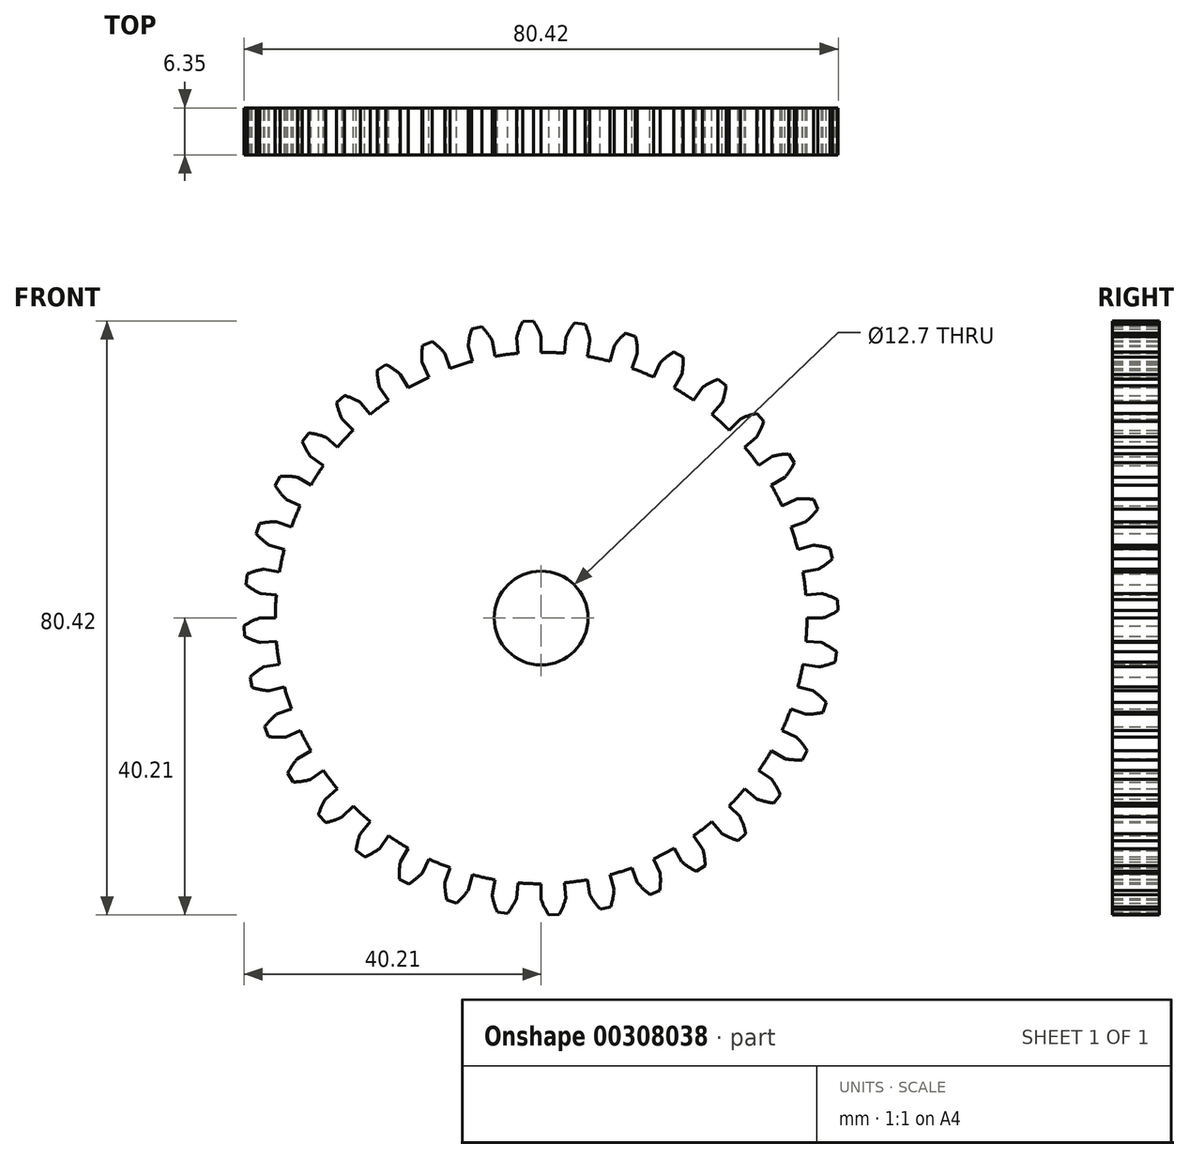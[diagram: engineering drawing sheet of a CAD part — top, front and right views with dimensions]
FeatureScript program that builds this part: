
annotation { "Feature Type Name" : "Feature", "Feature Type Description" : "" }
export const myFeature = defineFeature(function(context is Context, id is Id, definition is map)
    precondition{}
    {
        {
            var Q0;
            Q0=qCreatedBy(makeId("Front.planeOp"),FACE);
            var sketch = newSketch(context, id + "F0", { "sketchPlane" : qUnion([Q0])});
            skArc(sketch, "E0", {"start": v(-3.14, 35.84) * mm, "mid": v(-4.7, 35.67) * mm, "end": v(-6.25, 35.43) * mm});
            skPoint(sketch, "E1.endSnap0", {"position": v(0, 38.41) * mm});
            skArc(sketch, "E2.trimOffspring", {"start": v(0, 38.1) * mm, "mid": v(-0.46, 39.19) * mm, "end": v(-1.04, 40.2) * mm});
            skLineSegment(sketch, "E3", {"start": v(0, 38.1) * mm, "end": v(0, 35.98) * mm});
            skLineSegment(sketch, "E4", {"start": v(-1.04, 40.2) * mm, "end": v(-1.75, 40.18) * mm});
            skLineSegment(sketch, "E5.MirrorCS", {"start": v(-2.46, 40.15) * mm, "end": v(-1.75, 40.18) * mm});
            skArc(sketch, "E6.MirrorCS", {"start": v(-3.32, 37.96) * mm, "mid": v(-2.96, 39.08) * mm, "end": v(-2.46, 40.15) * mm});
            skLineSegment(sketch, "E7.MirrorCS", {"start": v(-3.32, 37.96) * mm, "end": v(-3.14, 35.84) * mm});
            skLineSegment(sketch, "E8.1.0", {"start": v(-9.86, 36.8) * mm, "end": v(-9.31, 34.75) * mm});
            skArc(sketch, "E8.1.1", {"start": v(-9.86, 36.8) * mm, "mid": v(-9.7, 37.97) * mm, "end": v(-9.4, 39.1) * mm});
            skLineSegment(sketch, "E8.1.2", {"start": v(-9.4, 39.1) * mm, "end": v(-8.7, 39.26) * mm});
            skLineSegment(sketch, "E8.1.3", {"start": v(-8.01, 39.42) * mm, "end": v(-8.7, 39.26) * mm});
            skArc(sketch, "E8.1.4", {"start": v(-6.62, 37.52) * mm, "mid": v(-7.25, 38.51) * mm, "end": v(-8.01, 39.42) * mm});
            skLineSegment(sketch, "E8.1.5", {"start": v(-6.62, 37.52) * mm, "end": v(-6.25, 35.43) * mm});
            skLineSegment(sketch, "E8.2.0", {"start": v(-16.1, 34.53) * mm, "end": v(-15.2, 32.6) * mm});
            skArc(sketch, "E8.2.1", {"start": v(-16.1, 34.53) * mm, "mid": v(-16.15, 35.7) * mm, "end": v(-16.05, 36.88) * mm});
            skLineSegment(sketch, "E8.2.2", {"start": v(-16.05, 36.88) * mm, "end": v(-15.39, 37.15) * mm});
            skLineSegment(sketch, "E8.2.3", {"start": v(-14.73, 37.43) * mm, "end": v(-15.39, 37.15) * mm});
            skArc(sketch, "E8.2.4", {"start": v(-13.03, 35.8) * mm, "mid": v(-13.83, 36.67) * mm, "end": v(-14.73, 37.43) * mm});
            skLineSegment(sketch, "E8.2.5", {"start": v(-13.03, 35.8) * mm, "end": v(-12.3, 33.8) * mm});
            skLineSegment(sketch, "E8.3.0", {"start": v(-21.85, 31.2) * mm, "end": v(-20.64, 29.47) * mm});
            skArc(sketch, "E8.3.1", {"start": v(-21.85, 31.2) * mm, "mid": v(-22.1, 32.36) * mm, "end": v(-22.2, 33.54) * mm});
            skLineSegment(sketch, "E8.3.2", {"start": v(-22.2, 33.54) * mm, "end": v(-21.6, 33.92) * mm});
            skLineSegment(sketch, "E8.3.3", {"start": v(-21, 34.3) * mm, "end": v(-21.6, 33.92) * mm});
            skArc(sketch, "E8.3.4", {"start": v(-19.05, 33) * mm, "mid": v(-19.99, 33.7) * mm, "end": v(-21, 34.3) * mm});
            skLineSegment(sketch, "E8.3.5", {"start": v(-19.05, 33) * mm, "end": v(-17.99, 31.16) * mm});
            skLineSegment(sketch, "E8.4.0", {"start": v(-26.94, 26.94) * mm, "end": v(-25.44, 25.44) * mm});
            skArc(sketch, "E8.4.1", {"start": v(-26.94, 26.94) * mm, "mid": v(-27.39, 28.03) * mm, "end": v(-27.7, 29.17) * mm});
            skLineSegment(sketch, "E8.4.2", {"start": v(-27.7, 29.17) * mm, "end": v(-27.17, 29.65) * mm});
            skLineSegment(sketch, "E8.4.3", {"start": v(-26.64, 30.13) * mm, "end": v(-27.17, 29.65) * mm});
            skArc(sketch, "E8.4.4", {"start": v(-24.5, 29.19) * mm, "mid": v(-25.54, 29.72) * mm, "end": v(-26.64, 30.13) * mm});
            skLineSegment(sketch, "E8.4.5", {"start": v(-24.5, 29.19) * mm, "end": v(-23.13, 27.56) * mm});
            skLineSegment(sketch, "E8.5.0", {"start": v(-31.2, 21.85) * mm, "end": v(-29.47, 20.64) * mm});
            skArc(sketch, "E8.5.1", {"start": v(-31.2, 21.85) * mm, "mid": v(-31.84, 22.85) * mm, "end": v(-32.34, 23.92) * mm});
            skLineSegment(sketch, "E8.5.2", {"start": v(-32.34, 23.92) * mm, "end": v(-31.9, 24.48) * mm});
            skLineSegment(sketch, "E8.5.3", {"start": v(-31.47, 25.04) * mm, "end": v(-31.9, 24.48) * mm});
            skArc(sketch, "E8.5.4", {"start": v(-29.19, 24.5) * mm, "mid": v(-30.31, 24.84) * mm, "end": v(-31.47, 25.04) * mm});
            skLineSegment(sketch, "E8.5.5", {"start": v(-29.19, 24.5) * mm, "end": v(-27.56, 23.13) * mm});
            skLineSegment(sketch, "E8.6.0", {"start": v(-34.53, 16.1) * mm, "end": v(-32.6, 15.2) * mm});
            skArc(sketch, "E8.6.1", {"start": v(-34.53, 16.1) * mm, "mid": v(-35.32, 16.97) * mm, "end": v(-36, 17.94) * mm});
            skLineSegment(sketch, "E8.6.2", {"start": v(-36, 17.94) * mm, "end": v(-35.67, 18.57) * mm});
            skLineSegment(sketch, "E8.6.3", {"start": v(-35.34, 19.2) * mm, "end": v(-35.67, 18.57) * mm});
            skArc(sketch, "E8.6.4", {"start": v(-33, 19.05) * mm, "mid": v(-34.16, 19.2) * mm, "end": v(-35.34, 19.2) * mm});
            skLineSegment(sketch, "E8.6.5", {"start": v(-33, 19.05) * mm, "end": v(-31.16, 17.99) * mm});
            skLineSegment(sketch, "E8.7.0", {"start": v(-36.8, 9.86) * mm, "end": v(-34.75, 9.31) * mm});
            skArc(sketch, "E8.7.1", {"start": v(-36.8, 9.86) * mm, "mid": v(-37.73, 10.58) * mm, "end": v(-38.57, 11.42) * mm});
            skLineSegment(sketch, "E8.7.2", {"start": v(-38.57, 11.42) * mm, "end": v(-38.35, 12.1) * mm});
            skLineSegment(sketch, "E8.7.3", {"start": v(-38.14, 12.77) * mm, "end": v(-38.35, 12.1) * mm});
            skArc(sketch, "E8.7.4", {"start": v(-35.8, 13.03) * mm, "mid": v(-36.98, 12.97) * mm, "end": v(-38.14, 12.77) * mm});
            skLineSegment(sketch, "E8.7.5", {"start": v(-35.8, 13.03) * mm, "end": v(-33.8, 12.3) * mm});
            skLineSegment(sketch, "E8.8.0", {"start": v(-37.96, 3.32) * mm, "end": v(-35.84, 3.14) * mm});
            skArc(sketch, "E8.8.1", {"start": v(-37.96, 3.32) * mm, "mid": v(-39, 3.87) * mm, "end": v(-39.96, 4.54) * mm});
            skLineSegment(sketch, "E8.8.2", {"start": v(-39.96, 4.54) * mm, "end": v(-39.87, 5.25) * mm});
            skLineSegment(sketch, "E8.8.3", {"start": v(-39.78, 5.95) * mm, "end": v(-39.87, 5.25) * mm});
            skArc(sketch, "E8.8.4", {"start": v(-37.52, 6.62) * mm, "mid": v(-38.67, 6.35) * mm, "end": v(-39.78, 5.95) * mm});
            skLineSegment(sketch, "E8.8.5", {"start": v(-37.52, 6.62) * mm, "end": v(-35.43, 6.25) * mm});
            skLineSegment(sketch, "E8.9.0", {"start": v(-37.96, -3.32) * mm, "end": v(-35.84, -3.14) * mm});
            skArc(sketch, "E8.9.1", {"start": v(-37.96, -3.32) * mm, "mid": v(-39.08, -2.96) * mm, "end": v(-40.15, -2.46) * mm});
            skLineSegment(sketch, "E8.9.2", {"start": v(-40.15, -2.46) * mm, "end": v(-40.18, -1.75) * mm});
            skLineSegment(sketch, "E8.9.3", {"start": v(-40.2, -1.04) * mm, "end": v(-40.18, -1.75) * mm});
            skArc(sketch, "E8.9.4", {"start": v(-38.1, 0) * mm, "mid": v(-39.19, -0.46) * mm, "end": v(-40.2, -1.04) * mm});
            skLineSegment(sketch, "E8.9.5", {"start": v(-38.1, 0) * mm, "end": v(-35.98, 0) * mm});
            skLineSegment(sketch, "E8.10.0", {"start": v(-36.8, -9.86) * mm, "end": v(-34.75, -9.31) * mm});
            skArc(sketch, "E8.10.1", {"start": v(-36.8, -9.86) * mm, "mid": v(-37.97, -9.7) * mm, "end": v(-39.1, -9.4) * mm});
            skLineSegment(sketch, "E8.10.2", {"start": v(-39.1, -9.4) * mm, "end": v(-39.26, -8.7) * mm});
            skLineSegment(sketch, "E8.10.3", {"start": v(-39.42, -8.01) * mm, "end": v(-39.26, -8.7) * mm});
            skArc(sketch, "E8.10.4", {"start": v(-37.52, -6.62) * mm, "mid": v(-38.51, -7.25) * mm, "end": v(-39.42, -8.01) * mm});
            skLineSegment(sketch, "E8.10.5", {"start": v(-37.52, -6.62) * mm, "end": v(-35.43, -6.25) * mm});
            skLineSegment(sketch, "E8.11.0", {"start": v(-34.53, -16.1) * mm, "end": v(-32.6, -15.2) * mm});
            skArc(sketch, "E8.11.1", {"start": v(-34.53, -16.1) * mm, "mid": v(-35.7, -16.15) * mm, "end": v(-36.88, -16.05) * mm});
            skLineSegment(sketch, "E8.11.2", {"start": v(-36.88, -16.05) * mm, "end": v(-37.15, -15.39) * mm});
            skLineSegment(sketch, "E8.11.3", {"start": v(-37.43, -14.73) * mm, "end": v(-37.15, -15.39) * mm});
            skArc(sketch, "E8.11.4", {"start": v(-35.8, -13.03) * mm, "mid": v(-36.67, -13.83) * mm, "end": v(-37.43, -14.73) * mm});
            skLineSegment(sketch, "E8.11.5", {"start": v(-35.8, -13.03) * mm, "end": v(-33.8, -12.3) * mm});
            skLineSegment(sketch, "E8.12.0", {"start": v(-31.2, -21.85) * mm, "end": v(-29.47, -20.64) * mm});
            skArc(sketch, "E8.12.1", {"start": v(-31.2, -21.85) * mm, "mid": v(-32.36, -22.1) * mm, "end": v(-33.54, -22.2) * mm});
            skLineSegment(sketch, "E8.12.2", {"start": v(-33.54, -22.2) * mm, "end": v(-33.92, -21.6) * mm});
            skLineSegment(sketch, "E8.12.3", {"start": v(-34.3, -21) * mm, "end": v(-33.92, -21.6) * mm});
            skArc(sketch, "E8.12.4", {"start": v(-33, -19.05) * mm, "mid": v(-33.7, -19.99) * mm, "end": v(-34.3, -21) * mm});
            skLineSegment(sketch, "E8.12.5", {"start": v(-33, -19.05) * mm, "end": v(-31.16, -17.99) * mm});
            skLineSegment(sketch, "E8.13.0", {"start": v(-26.94, -26.94) * mm, "end": v(-25.44, -25.44) * mm});
            skArc(sketch, "E8.13.1", {"start": v(-26.94, -26.94) * mm, "mid": v(-28.03, -27.39) * mm, "end": v(-29.17, -27.7) * mm});
            skLineSegment(sketch, "E8.13.2", {"start": v(-29.17, -27.7) * mm, "end": v(-29.65, -27.17) * mm});
            skLineSegment(sketch, "E8.13.3", {"start": v(-30.13, -26.64) * mm, "end": v(-29.65, -27.17) * mm});
            skArc(sketch, "E8.13.4", {"start": v(-29.19, -24.5) * mm, "mid": v(-29.72, -25.54) * mm, "end": v(-30.13, -26.64) * mm});
            skLineSegment(sketch, "E8.13.5", {"start": v(-29.19, -24.5) * mm, "end": v(-27.56, -23.13) * mm});
            skLineSegment(sketch, "E8.14.0", {"start": v(-21.85, -31.2) * mm, "end": v(-20.64, -29.47) * mm});
            skArc(sketch, "E8.14.1", {"start": v(-21.85, -31.2) * mm, "mid": v(-22.85, -31.84) * mm, "end": v(-23.92, -32.34) * mm});
            skLineSegment(sketch, "E8.14.2", {"start": v(-23.92, -32.34) * mm, "end": v(-24.48, -31.9) * mm});
            skLineSegment(sketch, "E8.14.3", {"start": v(-25.04, -31.47) * mm, "end": v(-24.48, -31.9) * mm});
            skArc(sketch, "E8.14.4", {"start": v(-24.5, -29.19) * mm, "mid": v(-24.84, -30.31) * mm, "end": v(-25.04, -31.47) * mm});
            skLineSegment(sketch, "E8.14.5", {"start": v(-24.5, -29.19) * mm, "end": v(-23.13, -27.56) * mm});
            skLineSegment(sketch, "E8.15.0", {"start": v(-16.1, -34.53) * mm, "end": v(-15.2, -32.6) * mm});
            skArc(sketch, "E8.15.1", {"start": v(-16.1, -34.53) * mm, "mid": v(-16.97, -35.32) * mm, "end": v(-17.94, -36) * mm});
            skLineSegment(sketch, "E8.15.2", {"start": v(-17.94, -36) * mm, "end": v(-18.57, -35.67) * mm});
            skLineSegment(sketch, "E8.15.3", {"start": v(-19.2, -35.34) * mm, "end": v(-18.57, -35.67) * mm});
            skArc(sketch, "E8.15.4", {"start": v(-19.05, -33) * mm, "mid": v(-19.2, -34.16) * mm, "end": v(-19.2, -35.34) * mm});
            skLineSegment(sketch, "E8.15.5", {"start": v(-19.05, -33) * mm, "end": v(-17.99, -31.16) * mm});
            skLineSegment(sketch, "E8.16.0", {"start": v(-9.86, -36.8) * mm, "end": v(-9.31, -34.75) * mm});
            skArc(sketch, "E8.16.1", {"start": v(-9.86, -36.8) * mm, "mid": v(-10.58, -37.73) * mm, "end": v(-11.42, -38.57) * mm});
            skLineSegment(sketch, "E8.16.2", {"start": v(-11.42, -38.57) * mm, "end": v(-12.1, -38.35) * mm});
            skLineSegment(sketch, "E8.16.3", {"start": v(-12.77, -38.14) * mm, "end": v(-12.1, -38.35) * mm});
            skArc(sketch, "E8.16.4", {"start": v(-13.03, -35.8) * mm, "mid": v(-12.97, -36.98) * mm, "end": v(-12.77, -38.14) * mm});
            skLineSegment(sketch, "E8.16.5", {"start": v(-13.03, -35.8) * mm, "end": v(-12.3, -33.8) * mm});
            skLineSegment(sketch, "E8.17.0", {"start": v(-3.32, -37.96) * mm, "end": v(-3.14, -35.84) * mm});
            skArc(sketch, "E8.17.1", {"start": v(-3.32, -37.96) * mm, "mid": v(-3.87, -39) * mm, "end": v(-4.54, -39.96) * mm});
            skLineSegment(sketch, "E8.17.2", {"start": v(-4.54, -39.96) * mm, "end": v(-5.25, -39.87) * mm});
            skLineSegment(sketch, "E8.17.3", {"start": v(-5.95, -39.78) * mm, "end": v(-5.25, -39.87) * mm});
            skArc(sketch, "E8.17.4", {"start": v(-6.62, -37.52) * mm, "mid": v(-6.35, -38.67) * mm, "end": v(-5.95, -39.78) * mm});
            skLineSegment(sketch, "E8.17.5", {"start": v(-6.62, -37.52) * mm, "end": v(-6.25, -35.43) * mm});
            skLineSegment(sketch, "E8.18.0", {"start": v(3.32, -37.96) * mm, "end": v(3.14, -35.84) * mm});
            skArc(sketch, "E8.18.1", {"start": v(3.32, -37.96) * mm, "mid": v(2.96, -39.08) * mm, "end": v(2.46, -40.15) * mm});
            skLineSegment(sketch, "E8.18.2", {"start": v(2.46, -40.15) * mm, "end": v(1.75, -40.18) * mm});
            skLineSegment(sketch, "E8.18.3", {"start": v(1.04, -40.2) * mm, "end": v(1.75, -40.18) * mm});
            skArc(sketch, "E8.18.4", {"start": v(0, -38.1) * mm, "mid": v(0.46, -39.19) * mm, "end": v(1.04, -40.2) * mm});
            skLineSegment(sketch, "E8.18.5", {"start": v(0, -38.1) * mm, "end": v(0, -35.98) * mm});
            skLineSegment(sketch, "E8.19.0", {"start": v(9.86, -36.8) * mm, "end": v(9.31, -34.75) * mm});
            skArc(sketch, "E8.19.1", {"start": v(9.86, -36.8) * mm, "mid": v(9.7, -37.97) * mm, "end": v(9.4, -39.1) * mm});
            skLineSegment(sketch, "E8.19.2", {"start": v(9.4, -39.1) * mm, "end": v(8.7, -39.26) * mm});
            skLineSegment(sketch, "E8.19.3", {"start": v(8.01, -39.42) * mm, "end": v(8.7, -39.26) * mm});
            skArc(sketch, "E8.19.4", {"start": v(6.62, -37.52) * mm, "mid": v(7.25, -38.51) * mm, "end": v(8.01, -39.42) * mm});
            skLineSegment(sketch, "E8.19.5", {"start": v(6.62, -37.52) * mm, "end": v(6.25, -35.43) * mm});
            skLineSegment(sketch, "E8.20.0", {"start": v(16.1, -34.53) * mm, "end": v(15.2, -32.6) * mm});
            skArc(sketch, "E8.20.1", {"start": v(16.1, -34.53) * mm, "mid": v(16.15, -35.7) * mm, "end": v(16.05, -36.88) * mm});
            skLineSegment(sketch, "E8.20.2", {"start": v(16.05, -36.88) * mm, "end": v(15.39, -37.15) * mm});
            skLineSegment(sketch, "E8.20.3", {"start": v(14.73, -37.43) * mm, "end": v(15.39, -37.15) * mm});
            skArc(sketch, "E8.20.4", {"start": v(13.03, -35.8) * mm, "mid": v(13.83, -36.67) * mm, "end": v(14.73, -37.43) * mm});
            skLineSegment(sketch, "E8.20.5", {"start": v(13.03, -35.8) * mm, "end": v(12.3, -33.8) * mm});
            skLineSegment(sketch, "E8.21.0", {"start": v(21.85, -31.2) * mm, "end": v(20.64, -29.47) * mm});
            skArc(sketch, "E8.21.1", {"start": v(21.85, -31.2) * mm, "mid": v(22.1, -32.36) * mm, "end": v(22.2, -33.54) * mm});
            skLineSegment(sketch, "E8.21.2", {"start": v(22.2, -33.54) * mm, "end": v(21.6, -33.92) * mm});
            skLineSegment(sketch, "E8.21.3", {"start": v(21, -34.3) * mm, "end": v(21.6, -33.92) * mm});
            skArc(sketch, "E8.21.4", {"start": v(19.05, -33) * mm, "mid": v(19.99, -33.7) * mm, "end": v(21, -34.3) * mm});
            skLineSegment(sketch, "E8.21.5", {"start": v(19.05, -33) * mm, "end": v(17.99, -31.16) * mm});
            skLineSegment(sketch, "E8.22.0", {"start": v(26.94, -26.94) * mm, "end": v(25.44, -25.44) * mm});
            skArc(sketch, "E8.22.1", {"start": v(26.94, -26.94) * mm, "mid": v(27.39, -28.03) * mm, "end": v(27.7, -29.17) * mm});
            skLineSegment(sketch, "E8.22.2", {"start": v(27.7, -29.17) * mm, "end": v(27.17, -29.65) * mm});
            skLineSegment(sketch, "E8.22.3", {"start": v(26.64, -30.13) * mm, "end": v(27.17, -29.65) * mm});
            skArc(sketch, "E8.22.4", {"start": v(24.5, -29.19) * mm, "mid": v(25.54, -29.72) * mm, "end": v(26.64, -30.13) * mm});
            skLineSegment(sketch, "E8.22.5", {"start": v(24.5, -29.19) * mm, "end": v(23.13, -27.56) * mm});
            skLineSegment(sketch, "E8.23.0", {"start": v(31.2, -21.85) * mm, "end": v(29.47, -20.64) * mm});
            skArc(sketch, "E8.23.1", {"start": v(31.2, -21.85) * mm, "mid": v(31.84, -22.85) * mm, "end": v(32.34, -23.92) * mm});
            skLineSegment(sketch, "E8.23.2", {"start": v(32.34, -23.92) * mm, "end": v(31.9, -24.48) * mm});
            skLineSegment(sketch, "E8.23.3", {"start": v(31.47, -25.04) * mm, "end": v(31.9, -24.48) * mm});
            skArc(sketch, "E8.23.4", {"start": v(29.19, -24.5) * mm, "mid": v(30.31, -24.84) * mm, "end": v(31.47, -25.04) * mm});
            skLineSegment(sketch, "E8.23.5", {"start": v(29.19, -24.5) * mm, "end": v(27.56, -23.13) * mm});
            skLineSegment(sketch, "E8.24.0", {"start": v(34.53, -16.1) * mm, "end": v(32.6, -15.2) * mm});
            skArc(sketch, "E8.24.1", {"start": v(34.53, -16.1) * mm, "mid": v(35.32, -16.97) * mm, "end": v(36, -17.94) * mm});
            skLineSegment(sketch, "E8.24.2", {"start": v(36, -17.94) * mm, "end": v(35.67, -18.57) * mm});
            skLineSegment(sketch, "E8.24.3", {"start": v(35.34, -19.2) * mm, "end": v(35.67, -18.57) * mm});
            skArc(sketch, "E8.24.4", {"start": v(33, -19.05) * mm, "mid": v(34.16, -19.2) * mm, "end": v(35.34, -19.2) * mm});
            skLineSegment(sketch, "E8.24.5", {"start": v(33, -19.05) * mm, "end": v(31.16, -17.99) * mm});
            skLineSegment(sketch, "E8.25.0", {"start": v(36.8, -9.86) * mm, "end": v(34.75, -9.31) * mm});
            skArc(sketch, "E8.25.1", {"start": v(36.8, -9.86) * mm, "mid": v(37.73, -10.58) * mm, "end": v(38.57, -11.42) * mm});
            skLineSegment(sketch, "E8.25.2", {"start": v(38.57, -11.42) * mm, "end": v(38.35, -12.1) * mm});
            skLineSegment(sketch, "E8.25.3", {"start": v(38.14, -12.77) * mm, "end": v(38.35, -12.1) * mm});
            skArc(sketch, "E8.25.4", {"start": v(35.8, -13.03) * mm, "mid": v(36.98, -12.97) * mm, "end": v(38.14, -12.77) * mm});
            skLineSegment(sketch, "E8.25.5", {"start": v(35.8, -13.03) * mm, "end": v(33.8, -12.3) * mm});
            skLineSegment(sketch, "E8.26.0", {"start": v(37.96, -3.32) * mm, "end": v(35.84, -3.14) * mm});
            skArc(sketch, "E8.26.1", {"start": v(37.96, -3.32) * mm, "mid": v(39, -3.87) * mm, "end": v(39.96, -4.54) * mm});
            skLineSegment(sketch, "E8.26.2", {"start": v(39.96, -4.54) * mm, "end": v(39.87, -5.25) * mm});
            skLineSegment(sketch, "E8.26.3", {"start": v(39.78, -5.95) * mm, "end": v(39.87, -5.25) * mm});
            skArc(sketch, "E8.26.4", {"start": v(37.52, -6.62) * mm, "mid": v(38.67, -6.35) * mm, "end": v(39.78, -5.95) * mm});
            skLineSegment(sketch, "E8.26.5", {"start": v(37.52, -6.62) * mm, "end": v(35.43, -6.25) * mm});
            skLineSegment(sketch, "E8.27.0", {"start": v(37.96, 3.32) * mm, "end": v(35.84, 3.14) * mm});
            skArc(sketch, "E8.27.1", {"start": v(37.96, 3.32) * mm, "mid": v(39.08, 2.96) * mm, "end": v(40.15, 2.46) * mm});
            skLineSegment(sketch, "E8.27.2", {"start": v(40.15, 2.46) * mm, "end": v(40.18, 1.75) * mm});
            skLineSegment(sketch, "E8.27.3", {"start": v(40.2, 1.04) * mm, "end": v(40.18, 1.75) * mm});
            skArc(sketch, "E8.27.4", {"start": v(38.1, 0) * mm, "mid": v(39.19, 0.46) * mm, "end": v(40.2, 1.04) * mm});
            skLineSegment(sketch, "E8.27.5", {"start": v(38.1, 0) * mm, "end": v(35.98, 0) * mm});
            skLineSegment(sketch, "E8.28.0", {"start": v(36.8, 9.86) * mm, "end": v(34.75, 9.31) * mm});
            skArc(sketch, "E8.28.1", {"start": v(36.8, 9.86) * mm, "mid": v(37.97, 9.7) * mm, "end": v(39.1, 9.4) * mm});
            skLineSegment(sketch, "E8.28.2", {"start": v(39.1, 9.4) * mm, "end": v(39.26, 8.7) * mm});
            skLineSegment(sketch, "E8.28.3", {"start": v(39.42, 8.01) * mm, "end": v(39.26, 8.7) * mm});
            skArc(sketch, "E8.28.4", {"start": v(37.52, 6.62) * mm, "mid": v(38.51, 7.25) * mm, "end": v(39.42, 8.01) * mm});
            skLineSegment(sketch, "E8.28.5", {"start": v(37.52, 6.62) * mm, "end": v(35.43, 6.25) * mm});
            skLineSegment(sketch, "E8.29.0", {"start": v(34.53, 16.1) * mm, "end": v(32.6, 15.2) * mm});
            skArc(sketch, "E8.29.1", {"start": v(34.53, 16.1) * mm, "mid": v(35.7, 16.15) * mm, "end": v(36.88, 16.05) * mm});
            skLineSegment(sketch, "E8.29.2", {"start": v(36.88, 16.05) * mm, "end": v(37.15, 15.39) * mm});
            skLineSegment(sketch, "E8.29.3", {"start": v(37.43, 14.73) * mm, "end": v(37.15, 15.39) * mm});
            skArc(sketch, "E8.29.4", {"start": v(35.8, 13.03) * mm, "mid": v(36.67, 13.83) * mm, "end": v(37.43, 14.73) * mm});
            skLineSegment(sketch, "E8.29.5", {"start": v(35.8, 13.03) * mm, "end": v(33.8, 12.3) * mm});
            skLineSegment(sketch, "E8.30.0", {"start": v(31.2, 21.85) * mm, "end": v(29.47, 20.64) * mm});
            skArc(sketch, "E8.30.1", {"start": v(31.2, 21.85) * mm, "mid": v(32.36, 22.1) * mm, "end": v(33.54, 22.2) * mm});
            skLineSegment(sketch, "E8.30.2", {"start": v(33.54, 22.2) * mm, "end": v(33.92, 21.6) * mm});
            skLineSegment(sketch, "E8.30.3", {"start": v(34.3, 21) * mm, "end": v(33.92, 21.6) * mm});
            skArc(sketch, "E8.30.4", {"start": v(33, 19.05) * mm, "mid": v(33.7, 19.99) * mm, "end": v(34.3, 21) * mm});
            skLineSegment(sketch, "E8.30.5", {"start": v(33, 19.05) * mm, "end": v(31.16, 17.99) * mm});
            skLineSegment(sketch, "E8.31.0", {"start": v(26.94, 26.94) * mm, "end": v(25.44, 25.44) * mm});
            skArc(sketch, "E8.31.1", {"start": v(26.94, 26.94) * mm, "mid": v(28.03, 27.39) * mm, "end": v(29.17, 27.7) * mm});
            skLineSegment(sketch, "E8.31.2", {"start": v(29.17, 27.7) * mm, "end": v(29.65, 27.17) * mm});
            skLineSegment(sketch, "E8.31.3", {"start": v(30.13, 26.64) * mm, "end": v(29.65, 27.17) * mm});
            skArc(sketch, "E8.31.4", {"start": v(29.19, 24.5) * mm, "mid": v(29.72, 25.54) * mm, "end": v(30.13, 26.64) * mm});
            skLineSegment(sketch, "E8.31.5", {"start": v(29.19, 24.5) * mm, "end": v(27.56, 23.13) * mm});
            skLineSegment(sketch, "E8.32.0", {"start": v(21.85, 31.2) * mm, "end": v(20.64, 29.47) * mm});
            skArc(sketch, "E8.32.1", {"start": v(21.85, 31.2) * mm, "mid": v(22.85, 31.84) * mm, "end": v(23.92, 32.34) * mm});
            skLineSegment(sketch, "E8.32.2", {"start": v(23.92, 32.34) * mm, "end": v(24.48, 31.9) * mm});
            skLineSegment(sketch, "E8.32.3", {"start": v(25.04, 31.47) * mm, "end": v(24.48, 31.9) * mm});
            skArc(sketch, "E8.32.4", {"start": v(24.5, 29.19) * mm, "mid": v(24.84, 30.31) * mm, "end": v(25.04, 31.47) * mm});
            skLineSegment(sketch, "E8.32.5", {"start": v(24.5, 29.19) * mm, "end": v(23.13, 27.56) * mm});
            skLineSegment(sketch, "E8.33.0", {"start": v(16.1, 34.53) * mm, "end": v(15.2, 32.6) * mm});
            skArc(sketch, "E8.33.1", {"start": v(16.1, 34.53) * mm, "mid": v(16.97, 35.32) * mm, "end": v(17.94, 36) * mm});
            skLineSegment(sketch, "E8.33.2", {"start": v(17.94, 36) * mm, "end": v(18.57, 35.67) * mm});
            skLineSegment(sketch, "E8.33.3", {"start": v(19.2, 35.34) * mm, "end": v(18.57, 35.67) * mm});
            skArc(sketch, "E8.33.4", {"start": v(19.05, 33) * mm, "mid": v(19.2, 34.16) * mm, "end": v(19.2, 35.34) * mm});
            skLineSegment(sketch, "E8.33.5", {"start": v(19.05, 33) * mm, "end": v(17.99, 31.16) * mm});
            skLineSegment(sketch, "E8.34.0", {"start": v(9.86, 36.8) * mm, "end": v(9.31, 34.75) * mm});
            skArc(sketch, "E8.34.1", {"start": v(9.86, 36.8) * mm, "mid": v(10.58, 37.73) * mm, "end": v(11.42, 38.57) * mm});
            skLineSegment(sketch, "E8.34.2", {"start": v(11.42, 38.57) * mm, "end": v(12.1, 38.35) * mm});
            skLineSegment(sketch, "E8.34.3", {"start": v(12.77, 38.14) * mm, "end": v(12.1, 38.35) * mm});
            skArc(sketch, "E8.34.4", {"start": v(13.03, 35.8) * mm, "mid": v(12.97, 36.98) * mm, "end": v(12.77, 38.14) * mm});
            skLineSegment(sketch, "E8.34.5", {"start": v(13.03, 35.8) * mm, "end": v(12.3, 33.8) * mm});
            skLineSegment(sketch, "E8.35.0", {"start": v(3.32, 37.96) * mm, "end": v(3.14, 35.84) * mm});
            skArc(sketch, "E8.35.1", {"start": v(3.32, 37.96) * mm, "mid": v(3.87, 39) * mm, "end": v(4.54, 39.96) * mm});
            skLineSegment(sketch, "E8.35.2", {"start": v(4.54, 39.96) * mm, "end": v(5.25, 39.87) * mm});
            skLineSegment(sketch, "E8.35.3", {"start": v(5.95, 39.78) * mm, "end": v(5.25, 39.87) * mm});
            skArc(sketch, "E8.35.4", {"start": v(6.62, 37.52) * mm, "mid": v(6.35, 38.67) * mm, "end": v(5.95, 39.78) * mm});
            skLineSegment(sketch, "E8.35.5", {"start": v(6.62, 37.52) * mm, "end": v(6.25, 35.43) * mm});
            skArc(sketch, "E9.trimOffspring", {"start": v(3.14, 35.84) * mm, "mid": v(1.57, 35.94) * mm, "end": v(0, 35.98) * mm});
            skArc(sketch, "E10.trimOffspring", {"start": v(-9.31, 34.75) * mm, "mid": v(-10.82, 34.31) * mm, "end": v(-12.3, 33.8) * mm});
            skArc(sketch, "E11.trimOffspring", {"start": v(-20.64, 29.47) * mm, "mid": v(-21.9, 28.54) * mm, "end": v(-23.13, 27.56) * mm});
            skArc(sketch, "E12.trimOffspring", {"start": v(15.2, 32.6) * mm, "mid": v(13.77, 33.24) * mm, "end": v(12.3, 33.8) * mm});
            skLineSegment(sketch, "E13", {"start": v(-17.99, 31.16) * mm, "end": v(-15.2, 32.6) * mm});
            skArc(sketch, "E14.trimOffspring", {"start": v(-25.44, 25.44) * mm, "mid": v(-26.53, 24.3) * mm, "end": v(-27.56, 23.13) * mm});
            skArc(sketch, "E15.trimOffspring", {"start": v(-29.47, 20.64) * mm, "mid": v(-30.34, 19.33) * mm, "end": v(-31.16, 17.99) * mm});
            skArc(sketch, "E16.trimOffspring", {"start": v(-32.6, 15.2) * mm, "mid": v(-33.24, 13.77) * mm, "end": v(-33.8, 12.3) * mm});
            skArc(sketch, "E17.trimOffspring", {"start": v(-34.75, 9.31) * mm, "mid": v(-35.13, 7.79) * mm, "end": v(-35.43, 6.25) * mm});
            skArc(sketch, "E18.trimOffspring", {"start": v(-35.84, 3.14) * mm, "mid": v(-35.94, 1.57) * mm, "end": v(-35.98, 0) * mm});
            skArc(sketch, "E19.trimOffspring", {"start": v(-35.84, -3.14) * mm, "mid": v(-35.67, -4.7) * mm, "end": v(-35.43, -6.25) * mm});
            skArc(sketch, "E20.trimOffspring", {"start": v(-34.75, -9.31) * mm, "mid": v(-34.31, -10.82) * mm, "end": v(-33.8, -12.3) * mm});
            skArc(sketch, "E21.trimOffspring", {"start": v(-32.6, -15.2) * mm, "mid": v(-31.91, -16.61) * mm, "end": v(-31.16, -17.99) * mm});
            skArc(sketch, "E22.trimOffspring", {"start": v(-29.47, -20.64) * mm, "mid": v(-28.54, -21.9) * mm, "end": v(-27.56, -23.13) * mm});
            skArc(sketch, "E23.trimOffspring", {"start": v(-25.44, -25.44) * mm, "mid": v(-24.3, -26.53) * mm, "end": v(-23.13, -27.56) * mm});
            skArc(sketch, "E24.trimOffspring", {"start": v(-20.64, -29.47) * mm, "mid": v(-19.33, -30.34) * mm, "end": v(-17.99, -31.16) * mm});
            skArc(sketch, "E25.trimOffspring", {"start": v(-15.2, -32.6) * mm, "mid": v(-13.77, -33.24) * mm, "end": v(-12.3, -33.8) * mm});
            skArc(sketch, "E26.trimOffspring", {"start": v(-9.31, -34.75) * mm, "mid": v(-7.79, -35.13) * mm, "end": v(-6.25, -35.43) * mm});
            skArc(sketch, "E27.trimOffspring", {"start": v(-3.14, -35.84) * mm, "mid": v(-1.57, -35.94) * mm, "end": v(0, -35.98) * mm});
            skArc(sketch, "E28.trimOffspring", {"start": v(3.14, -35.84) * mm, "mid": v(4.7, -35.67) * mm, "end": v(6.25, -35.43) * mm});
            skArc(sketch, "E29.trimOffspring", {"start": v(9.31, -34.75) * mm, "mid": v(10.82, -34.31) * mm, "end": v(12.3, -33.8) * mm});
            skArc(sketch, "E30.trimOffspring", {"start": v(20.64, -29.47) * mm, "mid": v(21.9, -28.54) * mm, "end": v(23.13, -27.56) * mm});
            skLineSegment(sketch, "E31", {"start": v(15.2, -32.6) * mm, "end": v(17.99, -31.16) * mm});
            skArc(sketch, "E32.trimOffspring", {"start": v(25.44, -25.44) * mm, "mid": v(26.53, -24.3) * mm, "end": v(27.56, -23.13) * mm});
            skArc(sketch, "E33.trimOffspring", {"start": v(29.47, -20.64) * mm, "mid": v(30.34, -19.33) * mm, "end": v(31.16, -17.99) * mm});
            skArc(sketch, "E34.trimOffspring", {"start": v(32.6, -15.2) * mm, "mid": v(33.24, -13.77) * mm, "end": v(33.8, -12.3) * mm});
            skArc(sketch, "E35.trimOffspring", {"start": v(34.75, -9.31) * mm, "mid": v(35.13, -7.79) * mm, "end": v(35.43, -6.25) * mm});
            skArc(sketch, "E36.trimOffspring", {"start": v(35.84, -3.14) * mm, "mid": v(35.94, -1.57) * mm, "end": v(35.98, 0) * mm});
            skArc(sketch, "E37.trimOffspring", {"start": v(29.47, 20.64) * mm, "mid": v(28.54, 21.9) * mm, "end": v(27.56, 23.13) * mm});
            skArc(sketch, "E38.trimOffspring", {"start": v(20.64, 29.47) * mm, "mid": v(19.33, 30.34) * mm, "end": v(17.99, 31.16) * mm});
            skArc(sketch, "E39.trimOffspring", {"start": v(35.84, 3.14) * mm, "mid": v(35.67, 4.7) * mm, "end": v(35.43, 6.25) * mm});
            skArc(sketch, "E40.trimOffspring", {"start": v(32.6, 15.2) * mm, "mid": v(31.91, 16.61) * mm, "end": v(31.16, 17.99) * mm});
            skArc(sketch, "E41.trimOffspring", {"start": v(34.75, 9.31) * mm, "mid": v(34.31, 10.82) * mm, "end": v(33.8, 12.3) * mm});
            skArc(sketch, "E42.trimOffspring", {"start": v(25.44, 25.44) * mm, "mid": v(24.3, 26.53) * mm, "end": v(23.13, 27.56) * mm});
            skArc(sketch, "E43.trimOffspring", {"start": v(9.31, 34.75) * mm, "mid": v(7.79, 35.13) * mm, "end": v(6.25, 35.43) * mm});
            skSolve(sketch);
        }
        {
            var Q0;
            Q0=makeQuery(id+"F0.imprint","IMPRINT",FACE,{"disambiguationData":[TD([[makeQuery(id+"F0.imprint","IMPRINT",EDGE,{"derivedFrom":sQuery(id+"F0.wireOp",EDGE,"E0")}),1.0]])]});
            extrude(context, id + "F1", {"entities" : qUnion([Q0]), "depth" : 6.35 * mm});
        }
        {
            var Q0;
            Q0=makeQuery(id+"F1.opExtrude","CAP_FACE",FACE,{"disambiguationData":[OSD([sQuery(id+"F0.wireOp",EDGE,"E0"),sQuery(id+"F0.wireOp",EDGE,"E2.trimOffspring"),sQuery(id+"F0.wireOp",EDGE,"E3"),sQuery(id+"F0.wireOp",EDGE,"E4"),sQuery(id+"F0.wireOp",EDGE,"E5.MirrorCS"),sQuery(id+"F0.wireOp",EDGE,"E6.MirrorCS"),sQuery(id+"F0.wireOp",EDGE,"E7.MirrorCS"),sQuery(id+"F0.wireOp",EDGE,"E8.1.0"),sQuery(id+"F0.wireOp",EDGE,"E8.1.1"),sQuery(id+"F0.wireOp",EDGE,"E8.1.2"),sQuery(id+"F0.wireOp",EDGE,"E8.1.3"),sQuery(id+"F0.wireOp",EDGE,"E8.1.4"),sQuery(id+"F0.wireOp",EDGE,"E8.1.5"),sQuery(id+"F0.wireOp",EDGE,"E8.2.0"),sQuery(id+"F0.wireOp",EDGE,"E8.2.1"),sQuery(id+"F0.wireOp",EDGE,"E8.2.2"),sQuery(id+"F0.wireOp",EDGE,"E8.2.3"),sQuery(id+"F0.wireOp",EDGE,"E8.2.4"),sQuery(id+"F0.wireOp",EDGE,"E8.2.5"),sQuery(id+"F0.wireOp",EDGE,"E8.3.0"),sQuery(id+"F0.wireOp",EDGE,"E8.3.1"),sQuery(id+"F0.wireOp",EDGE,"E8.3.2"),sQuery(id+"F0.wireOp",EDGE,"E8.3.3"),sQuery(id+"F0.wireOp",EDGE,"E8.3.4"),sQuery(id+"F0.wireOp",EDGE,"E8.3.5"),sQuery(id+"F0.wireOp",EDGE,"E8.4.0"),sQuery(id+"F0.wireOp",EDGE,"E8.4.1"),sQuery(id+"F0.wireOp",EDGE,"E8.4.2"),sQuery(id+"F0.wireOp",EDGE,"E8.4.3"),sQuery(id+"F0.wireOp",EDGE,"E8.4.4"),sQuery(id+"F0.wireOp",EDGE,"E8.4.5"),sQuery(id+"F0.wireOp",EDGE,"E8.5.0"),sQuery(id+"F0.wireOp",EDGE,"E8.5.1"),sQuery(id+"F0.wireOp",EDGE,"E8.5.2"),sQuery(id+"F0.wireOp",EDGE,"E8.5.3"),sQuery(id+"F0.wireOp",EDGE,"E8.5.4"),sQuery(id+"F0.wireOp",EDGE,"E8.5.5"),sQuery(id+"F0.wireOp",EDGE,"E8.6.0"),sQuery(id+"F0.wireOp",EDGE,"E8.6.1"),sQuery(id+"F0.wireOp",EDGE,"E8.6.2"),sQuery(id+"F0.wireOp",EDGE,"E8.6.3"),sQuery(id+"F0.wireOp",EDGE,"E8.6.4"),sQuery(id+"F0.wireOp",EDGE,"E8.6.5"),sQuery(id+"F0.wireOp",EDGE,"E8.7.0"),sQuery(id+"F0.wireOp",EDGE,"E8.7.1"),sQuery(id+"F0.wireOp",EDGE,"E8.7.2"),sQuery(id+"F0.wireOp",EDGE,"E8.7.3"),sQuery(id+"F0.wireOp",EDGE,"E8.7.4"),sQuery(id+"F0.wireOp",EDGE,"E8.7.5"),sQuery(id+"F0.wireOp",EDGE,"E8.8.0"),sQuery(id+"F0.wireOp",EDGE,"E8.8.1"),sQuery(id+"F0.wireOp",EDGE,"E8.8.2"),sQuery(id+"F0.wireOp",EDGE,"E8.8.3"),sQuery(id+"F0.wireOp",EDGE,"E8.8.4"),sQuery(id+"F0.wireOp",EDGE,"E8.8.5"),sQuery(id+"F0.wireOp",EDGE,"E8.9.0"),sQuery(id+"F0.wireOp",EDGE,"E8.9.1"),sQuery(id+"F0.wireOp",EDGE,"E8.9.2"),sQuery(id+"F0.wireOp",EDGE,"E8.9.3"),sQuery(id+"F0.wireOp",EDGE,"E8.9.4"),sQuery(id+"F0.wireOp",EDGE,"E8.9.5"),sQuery(id+"F0.wireOp",EDGE,"E8.10.0"),sQuery(id+"F0.wireOp",EDGE,"E8.10.1"),sQuery(id+"F0.wireOp",EDGE,"E8.10.2"),sQuery(id+"F0.wireOp",EDGE,"E8.10.3"),sQuery(id+"F0.wireOp",EDGE,"E8.10.4"),sQuery(id+"F0.wireOp",EDGE,"E8.10.5"),sQuery(id+"F0.wireOp",EDGE,"E8.11.0"),sQuery(id+"F0.wireOp",EDGE,"E8.11.1"),sQuery(id+"F0.wireOp",EDGE,"E8.11.2"),sQuery(id+"F0.wireOp",EDGE,"E8.11.3"),sQuery(id+"F0.wireOp",EDGE,"E8.11.4"),sQuery(id+"F0.wireOp",EDGE,"E8.11.5"),sQuery(id+"F0.wireOp",EDGE,"E8.12.0"),sQuery(id+"F0.wireOp",EDGE,"E8.12.1"),sQuery(id+"F0.wireOp",EDGE,"E8.12.2"),sQuery(id+"F0.wireOp",EDGE,"E8.12.3"),sQuery(id+"F0.wireOp",EDGE,"E8.12.4"),sQuery(id+"F0.wireOp",EDGE,"E8.12.5"),sQuery(id+"F0.wireOp",EDGE,"E8.13.0"),sQuery(id+"F0.wireOp",EDGE,"E8.13.1"),sQuery(id+"F0.wireOp",EDGE,"E8.13.2"),sQuery(id+"F0.wireOp",EDGE,"E8.13.3"),sQuery(id+"F0.wireOp",EDGE,"E8.13.4"),sQuery(id+"F0.wireOp",EDGE,"E8.13.5"),sQuery(id+"F0.wireOp",EDGE,"E8.14.0"),sQuery(id+"F0.wireOp",EDGE,"E8.14.1"),sQuery(id+"F0.wireOp",EDGE,"E8.14.2"),sQuery(id+"F0.wireOp",EDGE,"E8.14.3"),sQuery(id+"F0.wireOp",EDGE,"E8.14.4"),sQuery(id+"F0.wireOp",EDGE,"E8.14.5"),sQuery(id+"F0.wireOp",EDGE,"E8.15.0"),sQuery(id+"F0.wireOp",EDGE,"E8.15.1"),sQuery(id+"F0.wireOp",EDGE,"E8.15.2"),sQuery(id+"F0.wireOp",EDGE,"E8.15.3"),sQuery(id+"F0.wireOp",EDGE,"E8.15.4"),sQuery(id+"F0.wireOp",EDGE,"E8.15.5"),sQuery(id+"F0.wireOp",EDGE,"E8.16.0"),sQuery(id+"F0.wireOp",EDGE,"E8.16.1"),sQuery(id+"F0.wireOp",EDGE,"E8.16.2"),sQuery(id+"F0.wireOp",EDGE,"E8.16.3"),sQuery(id+"F0.wireOp",EDGE,"E8.16.4"),sQuery(id+"F0.wireOp",EDGE,"E8.16.5"),sQuery(id+"F0.wireOp",EDGE,"E8.17.0"),sQuery(id+"F0.wireOp",EDGE,"E8.17.1"),sQuery(id+"F0.wireOp",EDGE,"E8.17.2"),sQuery(id+"F0.wireOp",EDGE,"E8.17.3"),sQuery(id+"F0.wireOp",EDGE,"E8.17.4"),sQuery(id+"F0.wireOp",EDGE,"E8.17.5"),sQuery(id+"F0.wireOp",EDGE,"E8.18.0"),sQuery(id+"F0.wireOp",EDGE,"E8.18.1"),sQuery(id+"F0.wireOp",EDGE,"E8.18.2"),sQuery(id+"F0.wireOp",EDGE,"E8.18.3"),sQuery(id+"F0.wireOp",EDGE,"E8.18.4"),sQuery(id+"F0.wireOp",EDGE,"E8.18.5"),sQuery(id+"F0.wireOp",EDGE,"E8.19.0"),sQuery(id+"F0.wireOp",EDGE,"E8.19.1"),sQuery(id+"F0.wireOp",EDGE,"E8.19.2"),sQuery(id+"F0.wireOp",EDGE,"E8.19.3"),sQuery(id+"F0.wireOp",EDGE,"E8.19.4"),sQuery(id+"F0.wireOp",EDGE,"E8.19.5"),sQuery(id+"F0.wireOp",EDGE,"E8.20.0"),sQuery(id+"F0.wireOp",EDGE,"E8.20.1"),sQuery(id+"F0.wireOp",EDGE,"E8.20.2"),sQuery(id+"F0.wireOp",EDGE,"E8.20.3"),sQuery(id+"F0.wireOp",EDGE,"E8.20.4"),sQuery(id+"F0.wireOp",EDGE,"E8.20.5"),sQuery(id+"F0.wireOp",EDGE,"E8.21.0"),sQuery(id+"F0.wireOp",EDGE,"E8.21.1"),sQuery(id+"F0.wireOp",EDGE,"E8.21.2"),sQuery(id+"F0.wireOp",EDGE,"E8.21.3"),sQuery(id+"F0.wireOp",EDGE,"E8.21.4"),sQuery(id+"F0.wireOp",EDGE,"E8.21.5"),sQuery(id+"F0.wireOp",EDGE,"E8.22.0"),sQuery(id+"F0.wireOp",EDGE,"E8.22.1"),sQuery(id+"F0.wireOp",EDGE,"E8.22.2"),sQuery(id+"F0.wireOp",EDGE,"E8.22.3"),sQuery(id+"F0.wireOp",EDGE,"E8.22.4"),sQuery(id+"F0.wireOp",EDGE,"E8.22.5"),sQuery(id+"F0.wireOp",EDGE,"E8.23.0"),sQuery(id+"F0.wireOp",EDGE,"E8.23.1"),sQuery(id+"F0.wireOp",EDGE,"E8.23.2"),sQuery(id+"F0.wireOp",EDGE,"E8.23.3"),sQuery(id+"F0.wireOp",EDGE,"E8.23.4"),sQuery(id+"F0.wireOp",EDGE,"E8.23.5"),sQuery(id+"F0.wireOp",EDGE,"E8.24.0"),sQuery(id+"F0.wireOp",EDGE,"E8.24.1"),sQuery(id+"F0.wireOp",EDGE,"E8.24.2"),sQuery(id+"F0.wireOp",EDGE,"E8.24.3"),sQuery(id+"F0.wireOp",EDGE,"E8.24.4"),sQuery(id+"F0.wireOp",EDGE,"E8.24.5"),sQuery(id+"F0.wireOp",EDGE,"E8.25.0"),sQuery(id+"F0.wireOp",EDGE,"E8.25.1"),sQuery(id+"F0.wireOp",EDGE,"E8.25.2"),sQuery(id+"F0.wireOp",EDGE,"E8.25.3"),sQuery(id+"F0.wireOp",EDGE,"E8.25.4"),sQuery(id+"F0.wireOp",EDGE,"E8.25.5"),sQuery(id+"F0.wireOp",EDGE,"E8.26.0"),sQuery(id+"F0.wireOp",EDGE,"E8.26.1"),sQuery(id+"F0.wireOp",EDGE,"E8.26.2"),sQuery(id+"F0.wireOp",EDGE,"E8.26.3"),sQuery(id+"F0.wireOp",EDGE,"E8.26.4"),sQuery(id+"F0.wireOp",EDGE,"E8.26.5"),sQuery(id+"F0.wireOp",EDGE,"E8.27.0"),sQuery(id+"F0.wireOp",EDGE,"E8.27.1"),sQuery(id+"F0.wireOp",EDGE,"E8.27.2"),sQuery(id+"F0.wireOp",EDGE,"E8.27.3"),sQuery(id+"F0.wireOp",EDGE,"E8.27.4"),sQuery(id+"F0.wireOp",EDGE,"E8.27.5"),sQuery(id+"F0.wireOp",EDGE,"E8.28.0"),sQuery(id+"F0.wireOp",EDGE,"E8.28.1"),sQuery(id+"F0.wireOp",EDGE,"E8.28.2"),sQuery(id+"F0.wireOp",EDGE,"E8.28.3"),sQuery(id+"F0.wireOp",EDGE,"E8.28.4"),sQuery(id+"F0.wireOp",EDGE,"E8.28.5"),sQuery(id+"F0.wireOp",EDGE,"E8.29.0"),sQuery(id+"F0.wireOp",EDGE,"E8.29.1"),sQuery(id+"F0.wireOp",EDGE,"E8.29.2"),sQuery(id+"F0.wireOp",EDGE,"E8.29.3"),sQuery(id+"F0.wireOp",EDGE,"E8.29.4"),sQuery(id+"F0.wireOp",EDGE,"E8.29.5"),sQuery(id+"F0.wireOp",EDGE,"E8.30.0"),sQuery(id+"F0.wireOp",EDGE,"E8.30.1"),sQuery(id+"F0.wireOp",EDGE,"E8.30.2"),sQuery(id+"F0.wireOp",EDGE,"E8.30.3"),sQuery(id+"F0.wireOp",EDGE,"E8.30.4"),sQuery(id+"F0.wireOp",EDGE,"E8.30.5"),sQuery(id+"F0.wireOp",EDGE,"E8.31.0"),sQuery(id+"F0.wireOp",EDGE,"E8.31.1"),sQuery(id+"F0.wireOp",EDGE,"E8.31.2"),sQuery(id+"F0.wireOp",EDGE,"E8.31.3"),sQuery(id+"F0.wireOp",EDGE,"E8.31.4"),sQuery(id+"F0.wireOp",EDGE,"E8.31.5"),sQuery(id+"F0.wireOp",EDGE,"E8.32.0"),sQuery(id+"F0.wireOp",EDGE,"E8.32.1"),sQuery(id+"F0.wireOp",EDGE,"E8.32.2"),sQuery(id+"F0.wireOp",EDGE,"E8.32.3"),sQuery(id+"F0.wireOp",EDGE,"E8.32.4"),sQuery(id+"F0.wireOp",EDGE,"E8.32.5"),sQuery(id+"F0.wireOp",EDGE,"E8.33.0"),sQuery(id+"F0.wireOp",EDGE,"E8.33.1"),sQuery(id+"F0.wireOp",EDGE,"E8.33.2"),sQuery(id+"F0.wireOp",EDGE,"E8.33.3"),sQuery(id+"F0.wireOp",EDGE,"E8.33.4"),sQuery(id+"F0.wireOp",EDGE,"E8.33.5"),sQuery(id+"F0.wireOp",EDGE,"E8.34.0"),sQuery(id+"F0.wireOp",EDGE,"E8.34.1"),sQuery(id+"F0.wireOp",EDGE,"E8.34.2"),sQuery(id+"F0.wireOp",EDGE,"E8.34.3"),sQuery(id+"F0.wireOp",EDGE,"E8.34.4"),sQuery(id+"F0.wireOp",EDGE,"E8.34.5"),sQuery(id+"F0.wireOp",EDGE,"E8.35.0"),sQuery(id+"F0.wireOp",EDGE,"E8.35.1"),sQuery(id+"F0.wireOp",EDGE,"E8.35.2"),sQuery(id+"F0.wireOp",EDGE,"E8.35.3"),sQuery(id+"F0.wireOp",EDGE,"E8.35.4"),sQuery(id+"F0.wireOp",EDGE,"E8.35.5"),sQuery(id+"F0.wireOp",EDGE,"E9.trimOffspring"),sQuery(id+"F0.wireOp",EDGE,"E10.trimOffspring"),sQuery(id+"F0.wireOp",EDGE,"E11.trimOffspring"),sQuery(id+"F0.wireOp",EDGE,"E12.trimOffspring"),sQuery(id+"F0.wireOp",EDGE,"E13"),sQuery(id+"F0.wireOp",EDGE,"E14.trimOffspring"),sQuery(id+"F0.wireOp",EDGE,"E15.trimOffspring"),sQuery(id+"F0.wireOp",EDGE,"E16.trimOffspring"),sQuery(id+"F0.wireOp",EDGE,"E17.trimOffspring"),sQuery(id+"F0.wireOp",EDGE,"E18.trimOffspring"),sQuery(id+"F0.wireOp",EDGE,"E19.trimOffspring"),sQuery(id+"F0.wireOp",EDGE,"E20.trimOffspring"),sQuery(id+"F0.wireOp",EDGE,"E21.trimOffspring"),sQuery(id+"F0.wireOp",EDGE,"E22.trimOffspring"),sQuery(id+"F0.wireOp",EDGE,"E23.trimOffspring"),sQuery(id+"F0.wireOp",EDGE,"E24.trimOffspring"),sQuery(id+"F0.wireOp",EDGE,"E25.trimOffspring"),sQuery(id+"F0.wireOp",EDGE,"E26.trimOffspring"),sQuery(id+"F0.wireOp",EDGE,"E27.trimOffspring"),sQuery(id+"F0.wireOp",EDGE,"E28.trimOffspring"),sQuery(id+"F0.wireOp",EDGE,"E29.trimOffspring"),sQuery(id+"F0.wireOp",EDGE,"E30.trimOffspring"),sQuery(id+"F0.wireOp",EDGE,"E31"),sQuery(id+"F0.wireOp",EDGE,"E32.trimOffspring"),sQuery(id+"F0.wireOp",EDGE,"E33.trimOffspring"),sQuery(id+"F0.wireOp",EDGE,"E34.trimOffspring"),sQuery(id+"F0.wireOp",EDGE,"E35.trimOffspring"),sQuery(id+"F0.wireOp",EDGE,"E36.trimOffspring"),sQuery(id+"F0.wireOp",EDGE,"E37.trimOffspring"),sQuery(id+"F0.wireOp",EDGE,"E38.trimOffspring"),sQuery(id+"F0.wireOp",EDGE,"E39.trimOffspring"),sQuery(id+"F0.wireOp",EDGE,"E40.trimOffspring"),sQuery(id+"F0.wireOp",EDGE,"E41.trimOffspring"),sQuery(id+"F0.wireOp",EDGE,"E42.trimOffspring"),sQuery(id+"F0.wireOp",EDGE,"E43.trimOffspring")])],"isStart":false});
            var sketch = newSketch(context, id + "F2", { "sketchPlane" : qUnion([Q0])});
            skCircle(sketch, "E44", {"center": v(0, 0) * mm, "radius": 6.35 * mm});
            skSolve(sketch);
        }
        {
            var Q0;
            Q0=makeQuery(id+"F2.imprint","IMPRINT",FACE,{"disambiguationData":[TD([[makeQuery(id+"F2.imprint","IMPRINT",EDGE,{"derivedFrom":sQuery(id+"F2.wireOp",EDGE,"E44")}),1.0]])]});
            extrude(context, id + "F3", {"entities" : qUnion([Q0]), "operationType" : NewBodyOperationType.REMOVE, "endBound" : BoundingType.THROUGH_ALL, "oppositeDirection" : true, "depth" : 25.4 * mm});
        }
    });
